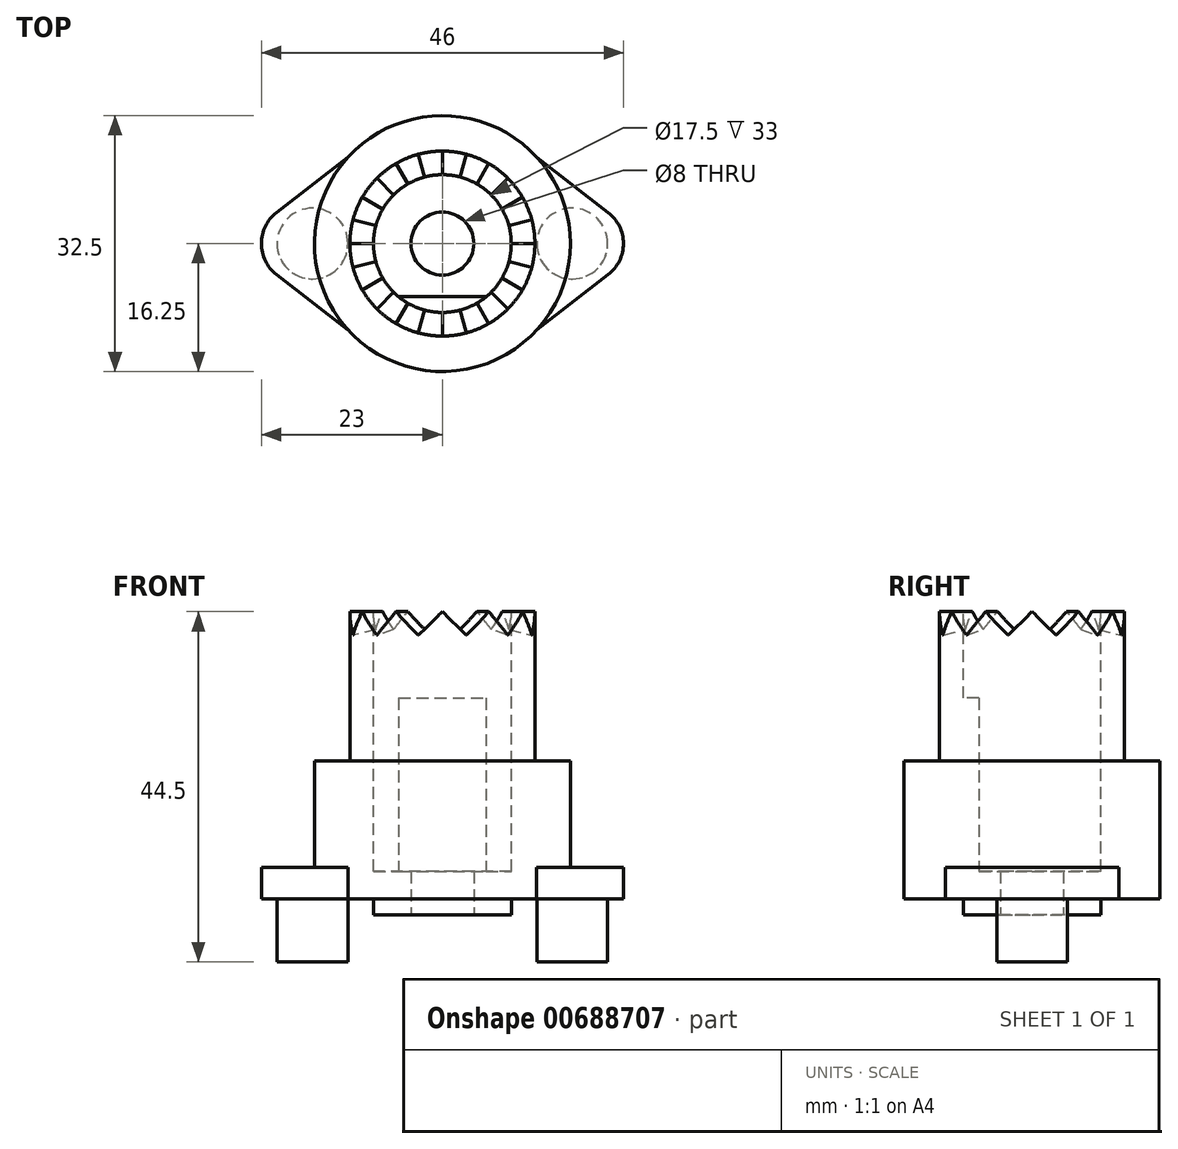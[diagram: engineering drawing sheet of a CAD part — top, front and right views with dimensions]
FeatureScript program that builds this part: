
annotation { "Feature Type Name" : "Feature", "Feature Type Description" : "" }
export const myFeature = defineFeature(function(context is Context, id is Id, definition is map)
    precondition{}
    {
        {
            var Q0;
            Q0=qCreatedBy(makeId("Top.planeOp"),FACE);
            var sketch = newSketch(context, id + "F0", { "sketchPlane" : qUnion([Q0])});
            skCircle(sketch, "E0", {"center": v(0, 0) * mm, "radius": 8.75 * mm});
            skSolve(sketch);
        }
        {
            var Q0;
            Q0 = qSketchRegion(id + "F0", true);
            extrude(context, id + "F1", {"entities" : qUnion([Q0]), "depth" : 2 * mm, "offsetDistance" : 25 * mm});
        }
        {
            var Q0;
            Q0=makeQuery(id+"F1.opExtrude","CAP_FACE",FACE,{"disambiguationData":[OSD([sQuery(id+"F0.wireOp",EDGE,"E0")])],"isStart":false});
            var sketch = newSketch(context, id + "F2", { "sketchPlane" : qUnion([Q0])});
            skCircle(sketch, "E1", {"center": v(0, 0) * mm, "radius": 16.25 * mm});
            skSolve(sketch);
        }
        {
            var Q0;
            Q0 = qSketchRegion(id + "F2", true);
            extrude(context, id + "F3", {"entities" : qUnion([Q0]), "operationType" : NewBodyOperationType.ADD, "depth" : 17.5 * mm, "offsetDistance" : 25 * mm});
        }
        {
            var Q0;
            Q0=makeQuery(id+"F3.opExtrude","CAP_FACE",FACE,{"disambiguationData":[OSD([sQuery(id+"F2.wireOp",EDGE,"E1")])],"isStart":false});
            var sketch = newSketch(context, id + "F4", { "sketchPlane" : qUnion([Q0])});
            skCircle(sketch, "E2", {"center": v(0, 0) * mm, "radius": 11.75 * mm});
            skSolve(sketch);
        }
        {
            var Q0;
            Q0=makeQuery(id+"F4.imprint","IMPRINT",FACE,{"disambiguationData":[TD([[makeQuery(id+"F4.imprint","IMPRINT",EDGE,{"derivedFrom":sQuery(id+"F4.wireOp",EDGE,"E2")}),1.0]])]});
            extrude(context, id + "F5", {"entities" : qUnion([Q0]), "operationType" : NewBodyOperationType.ADD, "depth" : 19 * mm, "offsetDistance" : 25 * mm});
        }
        {
            var Q0;
            Q0=makeQuery(id+"F5.opExtrude","CAP_FACE",FACE,{"disambiguationData":[OSD([sQuery(id+"F4.wireOp",EDGE,"E2")])],"isStart":false});
            var sketch = newSketch(context, id + "F6", { "sketchPlane" : qUnion([Q0])});
            skCircle(sketch, "E3", {"center": v(0, 0) * mm, "radius": 8.75 * mm});
            skSolve(sketch);
        }
        {
            var Q0;
            Q0=makeQuery(id+"F6.imprint","IMPRINT",FACE,{"disambiguationData":[TD([[makeQuery(id+"F6.imprint","IMPRINT",EDGE,{"derivedFrom":sQuery(id+"F6.wireOp",EDGE,"E3")}),1.0]])]});
            extrude(context, id + "F7", {"entities" : qUnion([Q0]), "operationType" : NewBodyOperationType.REMOVE, "oppositeDirection" : true, "depth" : 33 * mm, "offsetDistance" : 25 * mm});
        }
        {
            var Q0;
            Q0=makeQuery(id+"F1.opExtrude","CAP_FACE",FACE,{"disambiguationData":[OSD([sQuery(id+"F0.wireOp",EDGE,"E0")])],"isStart":true});
            var sketch = newSketch(context, id + "F8", { "sketchPlane" : qUnion([Q0])});
            skCircle(sketch, "E4", {"center": v(0, 0) * mm, "radius": 4 * mm});
            skSolve(sketch);
        }
        {
            var Q0;
            Q0=makeQuery(id+"F8.imprint","IMPRINT",FACE,{"disambiguationData":[TD([[makeQuery(id+"F8.imprint","IMPRINT",EDGE,{"derivedFrom":sQuery(id+"F8.wireOp",EDGE,"E4")}),1.0]])]});
            extrude(context, id + "F9", {"entities" : qUnion([Q0]), "operationType" : NewBodyOperationType.REMOVE, "endBound" : BoundingType.UP_TO_NEXT, "oppositeDirection" : true, "depth" : 25 * mm, "offsetDistance" : 25 * mm});
        }
        {
            var Q0;
            Q0=makeQuery(id+"F3.opExtrude","CAP_FACE",FACE,{"disambiguationData":[OSD([sQuery(id+"F2.wireOp",EDGE,"E1")])],"isStart":true});
            var sketch = newSketch(context, id + "F10", { "sketchPlane" : qUnion([Q0])});
            skLineSegment(sketch, "E5", {"start": v(-11.96, 11) * mm, "end": v(-21.06, 3.95) * mm});
            skLineSegment(sketch, "E6", {"start": v(-21.06, -3.95) * mm, "end": v(-11.96, -11) * mm});
            skArc(sketch, "E7.filletArc", {"start": v(-21.06, 3.95) * mm, "mid": v(-23, 0) * mm, "end": v(-21.06, -3.95) * mm});
            skLineSegment(sketch, "E8", {"start": v(11.96, -11) * mm, "end": v(21.06, -3.95) * mm});
            skLineSegment(sketch, "E9", {"start": v(21.06, 3.95) * mm, "end": v(11.96, 11) * mm});
            skArc(sketch, "E10.filletArc", {"start": v(21.06, -3.95) * mm, "mid": v(23, 0) * mm, "end": v(21.06, 3.95) * mm});
            skLineSegment(sketch, "E11", {"start": v(-18, 0) * mm, "end": v(0, 0) * mm, "construction": true});
            skArc(sketch, "E12", {"start": v(11.96, -11) * mm, "mid": v(16.25, 0) * mm, "end": v(11.96, 11) * mm});
            skArc(sketch, "E13", {"start": v(-11.96, 11) * mm, "mid": v(-16.25, 0) * mm, "end": v(-11.96, -11) * mm});
            skSolve(sketch);
        }
        {
            var Q0;
            {var subQ0=sQuery(id+"F10.wireOp",EDGE,"E7.filletArc");Q0=makeQuery(id+"F10.imprint","IMPRINT",FACE,{"disambiguationData":[TD([[makeQuery(id+"F10.imprint","IMPRINT",EDGE,{"derivedFrom":subQ0}),1.0]])]});}
            var Q1;
            {var subQ0=sQuery(id+"F10.wireOp",EDGE,"E10.filletArc");Q1=makeQuery(id+"F10.imprint","IMPRINT",FACE,{"disambiguationData":[TD([[makeQuery(id+"F10.imprint","IMPRINT",EDGE,{"derivedFrom":subQ0}),1.0]])]});}
            var Q2;
            Q2=sQuery(id+"F10.wireOp",EDGE,"E5");
            var Q3;
            Q3=sQuery(id+"F10.wireOp",EDGE,"E13");
            var Q4;
            Q4=sQuery(id+"F10.wireOp",EDGE,"E7.filletArc");
            var Q5;
            Q5=sQuery(id+"F10.wireOp",EDGE,"E6");
            extrude(context, id + "F11", {"entities" : qUnion([Q0, Q1]), "operationType" : NewBodyOperationType.ADD, "surfaceEntities" : qUnion([Q2, Q3, Q4, Q5]), "oppositeDirection" : true, "depth" : 4 * mm, "offsetDistance" : 25 * mm});
        }
        {
            var Q0;
            Q0=makeQuery(id+"F11.boolean.opBoolean","MERGE",FACE,{"derivedFrom":[makeQuery(id+"F3.opExtrude","CAP_FACE",FACE,{"disambiguationData":[OSD([sQuery(id+"F2.wireOp",EDGE,"E1")])],"isStart":true}),makeQuery(id+"F11.opExtrude","CAP_FACE",FACE,{"disambiguationData":[OSD([sQuery(id+"F10.wireOp",EDGE,"E5"),sQuery(id+"F10.wireOp",EDGE,"E6"),sQuery(id+"F10.wireOp",EDGE,"E7.filletArc"),sQuery(id+"F10.wireOp",EDGE,"E13")])],"isStart":true}),makeQuery(id+"F11.opExtrude","CAP_FACE",FACE,{"disambiguationData":[OSD([sQuery(id+"F10.wireOp",EDGE,"E8"),sQuery(id+"F10.wireOp",EDGE,"E9"),sQuery(id+"F10.wireOp",EDGE,"E10.filletArc"),sQuery(id+"F10.wireOp",EDGE,"E12")])],"isStart":true})]});
            var sketch = newSketch(context, id + "F12", { "sketchPlane" : qUnion([Q0])});
            skCircle(sketch, "E14", {"center": v(16.5, 0) * mm, "radius": 4.5 * mm});
            skLineSegment(sketch, "E15", {"start": v(23, 0) * mm, "end": v(-23, 0) * mm, "construction": true});
            skCircle(sketch, "E16.1.0", {"center": v(-16.5, 0) * mm, "radius": 4.5 * mm});
            skPoint(sketch, "E16.center", {"position": v(0, 0) * mm});
            skSolve(sketch);
        }
        {
            var Q0;
            Q0=makeQuery(id+"F12.imprint","IMPRINT",FACE,{"disambiguationData":[TD([[makeQuery(id+"F12.imprint","IMPRINT",EDGE,{"derivedFrom":sQuery(id+"F12.wireOp",EDGE,"E16.1.0")}),1.0]])]});
            var Q1;
            Q1=makeQuery(id+"F12.imprint","IMPRINT",FACE,{"disambiguationData":[TD([[makeQuery(id+"F12.imprint","IMPRINT",EDGE,{"derivedFrom":sQuery(id+"F12.wireOp",EDGE,"E14")}),1.0]])]});
            extrude(context, id + "F13", {"entities" : qUnion([Q0, Q1]), "operationType" : NewBodyOperationType.ADD, "depth" : 8 * mm, "offsetDistance" : 25 * mm});
        }
        {
            var Q0;
            Q0=makeQuery(id+"F7.boolean.opBoolean","COPY",FACE,{"derivedFrom":makeQuery(id+"F7.opExtrude","CAP_FACE",FACE,{"disambiguationData":[OSD([sQuery(id+"F6.wireOp",EDGE,"E3")])],"isStart":false})});
            var sketch = newSketch(context, id + "F14", { "sketchPlane" : qUnion([Q0])});
            skLineSegment(sketch, "E17", {"start": v(-5.57, -6.75) * mm, "end": v(5.57, -6.75) * mm});
            skSolve(sketch);
        }
        {
            var Q0;
            {var subQ0=sQuery(id+"F14.wireOp",EDGE,"E17");Q0=makeQuery(id+"F14.imprint","IMPRINT",FACE,{"disambiguationData":[TD([[makeQuery(id+"F14.imprint","IMPRINT",EDGE,{"derivedFrom":subQ0}),-1.0]])]});}
            extrude(context, id + "F15", {"entities" : qUnion([Q0]), "operationType" : NewBodyOperationType.ADD, "depth" : 22 * mm, "offsetDistance" : 25 * mm});
        }
        {
            var Q0;
            Q0=makeQuery(id+"F5.opExtrude","CAP_FACE",FACE,{"disambiguationData":[OSD([sQuery(id+"F4.wireOp",EDGE,"E2")])],"isStart":false});
            var sketch = newSketch(context, id + "F16", { "sketchPlane" : qUnion([Q0])});
            skLineSegment(sketch, "E18", {"start": v(-8.75, 0) * mm, "end": v(-11.75, 0) * mm});
            skLineSegment(sketch, "E19.1.0", {"start": v(-7.58, -4.37) * mm, "end": v(-10.18, -5.87) * mm});
            skLineSegment(sketch, "E19.2.0", {"start": v(-4.38, -7.58) * mm, "end": v(-5.88, -10.18) * mm});
            skLineSegment(sketch, "E19.3.0", {"start": v(0, -8.75) * mm, "end": v(0, -11.75) * mm});
            skLineSegment(sketch, "E19.4.0", {"start": v(4.37, -7.58) * mm, "end": v(5.87, -10.18) * mm});
            skLineSegment(sketch, "E19.5.0", {"start": v(7.58, -4.37) * mm, "end": v(10.18, -5.87) * mm});
            skLineSegment(sketch, "E19.6.0", {"start": v(8.75, 0) * mm, "end": v(11.75, 0) * mm});
            skLineSegment(sketch, "E19.7.0", {"start": v(7.58, 4.37) * mm, "end": v(10.18, 5.87) * mm});
            skLineSegment(sketch, "E19.8.0", {"start": v(4.38, 7.58) * mm, "end": v(5.88, 10.18) * mm});
            skLineSegment(sketch, "E19.9.0", {"start": v(0, 8.75) * mm, "end": v(0, 11.75) * mm});
            skLineSegment(sketch, "E19.10.0", {"start": v(-4.38, 7.58) * mm, "end": v(-5.88, 10.18) * mm});
            skLineSegment(sketch, "E19.11.0", {"start": v(-7.58, 4.38) * mm, "end": v(-10.18, 5.88) * mm});
            skPoint(sketch, "E19.center", {"position": v(0, 0) * mm});
            skSolve(sketch);
        }
        {
            var Q0;
            {var subQ0=sQuery(id+"F16.wireOp",EDGE,"E18");Q0=makeQuery(id+"F16.imprint","IMPRINT",FACE,{"disambiguationData":[TD([[makeQuery(id+"F16.imprint","IMPRINT",EDGE,{"derivedFrom":subQ0}),1.0]])]});}
            extrude(context, id + "F17", {"entities" : qUnion([Q0]), "operationType" : NewBodyOperationType.REMOVE, "oppositeDirection" : true, "depth" : 3 * mm, "offsetDistance" : 25 * mm});
        }
        {
            var Q0;
            Q0=makeQuery(id+"F17.boolean.opBoolean","COPY",EDGE,{"derivedFrom":makeQuery(id+"F17.opExtrude","CAP_EDGE",EDGE,{"disambiguationData":[OSD([sQuery(id+"F16.wireOp",EDGE,"E18")])],"isStart":false})});
            chamfer(context, id + "F18", {"entities" : qUnion([Q0]), "width" : 3 * mm, "tangentPropagation" : true});
        }
        {
            var Q0;
            Q0=makeQuery(id+"F17.boolean.opBoolean","COPY",EDGE,{"derivedFrom":makeQuery(id+"F17.opExtrude","CAP_EDGE",EDGE,{"disambiguationData":[OSD([sQuery(id+"F16.wireOp",EDGE,"E19.1.0")])],"isStart":false})});
            chamfer(context, id + "F19", {"entities" : qUnion([Q0]), "width" : 3 * mm, "tangentPropagation" : true});
        }
        {
            var Q0;
            {var subQ0=sQuery(id+"F16.wireOp",EDGE,"E19.10.0");Q0=makeQuery(id+"F16.imprint","IMPRINT",FACE,{"disambiguationData":[TD([[makeQuery(id+"F16.imprint","IMPRINT",EDGE,{"derivedFrom":subQ0}),1.0]])]});}
            var Q1;
            {var subQ0=sQuery(id+"F16.wireOp",EDGE,"E19.8.0");Q1=makeQuery(id+"F16.imprint","IMPRINT",FACE,{"disambiguationData":[TD([[makeQuery(id+"F16.imprint","IMPRINT",EDGE,{"derivedFrom":subQ0}),1.0]])]});}
            var Q2;
            {var subQ0=sQuery(id+"F16.wireOp",EDGE,"E19.6.0");Q2=makeQuery(id+"F16.imprint","IMPRINT",FACE,{"disambiguationData":[TD([[makeQuery(id+"F16.imprint","IMPRINT",EDGE,{"derivedFrom":subQ0}),1.0]])]});}
            var Q3;
            {var subQ0=sQuery(id+"F16.wireOp",EDGE,"E19.4.0");Q3=makeQuery(id+"F16.imprint","IMPRINT",FACE,{"disambiguationData":[TD([[makeQuery(id+"F16.imprint","IMPRINT",EDGE,{"derivedFrom":subQ0}),1.0]])]});}
            var Q4;
            {var subQ0=sQuery(id+"F16.wireOp",EDGE,"E19.2.0");Q4=makeQuery(id+"F16.imprint","IMPRINT",FACE,{"disambiguationData":[TD([[makeQuery(id+"F16.imprint","IMPRINT",EDGE,{"derivedFrom":subQ0}),1.0]])]});}
            extrude(context, id + "F20", {"entities" : qUnion([Q0, Q1, Q2, Q3, Q4]), "operationType" : NewBodyOperationType.REMOVE, "oppositeDirection" : true, "depth" : 3 * mm, "offsetDistance" : 25 * mm});
        }
        {
            var Q0;
            Q0=makeQuery(id+"F20.boolean.opBoolean","COPY",EDGE,{"derivedFrom":makeQuery(id+"F20.opExtrude","CAP_EDGE",EDGE,{"disambiguationData":[OSD([sQuery(id+"F16.wireOp",EDGE,"E19.8.0")])],"isStart":false})});
            var Q1;
            Q1=makeQuery(id+"F20.boolean.opBoolean","COPY",EDGE,{"derivedFrom":makeQuery(id+"F20.opExtrude","CAP_EDGE",EDGE,{"disambiguationData":[OSD([sQuery(id+"F16.wireOp",EDGE,"E19.5.0")])],"isStart":false})});
            var Q2;
            Q2=makeQuery(id+"F20.boolean.opBoolean","COPY",EDGE,{"derivedFrom":makeQuery(id+"F20.opExtrude","CAP_EDGE",EDGE,{"disambiguationData":[OSD([sQuery(id+"F16.wireOp",EDGE,"E19.3.0")])],"isStart":false})});
            var Q3;
            Q3=makeQuery(id+"F20.boolean.opBoolean","COPY",EDGE,{"derivedFrom":makeQuery(id+"F20.opExtrude","CAP_EDGE",EDGE,{"disambiguationData":[OSD([sQuery(id+"F16.wireOp",EDGE,"E19.10.0")])],"isStart":false})});
            chamfer(context, id + "F21", {"entities" : qUnion([Q0, Q1, Q2, Q3]), "width" : 3 * mm, "tangentPropagation" : true});
        }
        {
            var Q0;
            Q0=makeQuery(id+"F20.boolean.opBoolean","COPY",EDGE,{"derivedFrom":makeQuery(id+"F20.opExtrude","CAP_EDGE",EDGE,{"disambiguationData":[OSD([sQuery(id+"F16.wireOp",EDGE,"E19.6.0")])],"isStart":false})});
            var Q1;
            Q1=makeQuery(id+"F20.boolean.opBoolean","COPY",EDGE,{"derivedFrom":makeQuery(id+"F20.opExtrude","CAP_EDGE",EDGE,{"disambiguationData":[OSD([sQuery(id+"F16.wireOp",EDGE,"E19.4.0")])],"isStart":false})});
            var Q2;
            Q2=makeQuery(id+"F20.boolean.opBoolean","COPY",EDGE,{"derivedFrom":makeQuery(id+"F20.opExtrude","CAP_EDGE",EDGE,{"disambiguationData":[OSD([sQuery(id+"F16.wireOp",EDGE,"E19.11.0")])],"isStart":false})});
            chamfer(context, id + "F22", {"entities" : qUnion([Q0, Q1, Q2]), "width" : 3 * mm, "tangentPropagation" : true});
        }
        {
            var Q0;
            Q0=makeQuery(id+"F20.boolean.opBoolean","COPY",EDGE,{"derivedFrom":makeQuery(id+"F20.opExtrude","CAP_EDGE",EDGE,{"disambiguationData":[OSD([sQuery(id+"F16.wireOp",EDGE,"E19.9.0")])],"isStart":false})});
            var Q1;
            Q1=makeQuery(id+"F20.boolean.opBoolean","COPY",EDGE,{"derivedFrom":makeQuery(id+"F20.opExtrude","CAP_EDGE",EDGE,{"disambiguationData":[OSD([sQuery(id+"F16.wireOp",EDGE,"E19.7.0")])],"isStart":false})});
            chamfer(context, id + "F23", {"entities" : qUnion([Q0, Q1]), "width" : 3 * mm, "tangentPropagation" : true});
        }
        {
            var Q0;
            Q0=makeQuery(id+"F20.boolean.opBoolean","COPY",EDGE,{"derivedFrom":makeQuery(id+"F20.opExtrude","CAP_EDGE",EDGE,{"disambiguationData":[OSD([sQuery(id+"F16.wireOp",EDGE,"E19.2.0")])],"isStart":false})});
            chamfer(context, id + "F24", {"entities" : qUnion([Q0]), "width" : 3 * mm, "tangentPropagation" : true});
        }
        {
            var Q0;
            {var subQ0=sQuery(id+"F4.wireOp",EDGE,"E2");Q0=makeQuery(id+"F20.boolean.opBoolean","SPLIT",FACE,{"disambiguationData":[TD([makeQuery(id+"F19.opChamfer","BLEND_FACE",FACE,{"disambiguationData":[OSD([sQuery(id+"F16.wireOp",EDGE,"E19.1.0")])]})])],"derivedFrom":makeQuery(id+"F5.opExtrude","CAP_FACE",FACE,{"disambiguationData":[OSD([subQ0])],"isStart":false})});}
            var Q1;
            {var subQ0=sQuery(id+"F4.wireOp",EDGE,"E2");Q1=makeQuery(id+"F20.boolean.opBoolean","SPLIT",FACE,{"disambiguationData":[TD([makeQuery(id+"F20.opExtrude","SWEPT_FACE",FACE,{"disambiguationData":[OSD([sQuery(id+"F16.wireOp",EDGE,"E19.3.0")])]})])],"derivedFrom":makeQuery(id+"F5.opExtrude","CAP_FACE",FACE,{"disambiguationData":[OSD([subQ0])],"isStart":false})});}
            var Q2;
            {var subQ0=sQuery(id+"F4.wireOp",EDGE,"E2");Q2=makeQuery(id+"F20.boolean.opBoolean","SPLIT",FACE,{"disambiguationData":[TD([makeQuery(id+"F20.opExtrude","SWEPT_FACE",FACE,{"disambiguationData":[OSD([sQuery(id+"F16.wireOp",EDGE,"E19.5.0")])]})])],"derivedFrom":makeQuery(id+"F5.opExtrude","CAP_FACE",FACE,{"disambiguationData":[OSD([subQ0])],"isStart":false})});}
            var Q3;
            {var subQ0=sQuery(id+"F4.wireOp",EDGE,"E2");Q3=makeQuery(id+"F20.boolean.opBoolean","SPLIT",FACE,{"disambiguationData":[TD([makeQuery(id+"F20.opExtrude","SWEPT_FACE",FACE,{"disambiguationData":[OSD([sQuery(id+"F16.wireOp",EDGE,"E19.7.0")])]})])],"derivedFrom":makeQuery(id+"F5.opExtrude","CAP_FACE",FACE,{"disambiguationData":[OSD([subQ0])],"isStart":false})});}
            var Q4;
            {var subQ0=sQuery(id+"F4.wireOp",EDGE,"E2");Q4=makeQuery(id+"F20.boolean.opBoolean","SPLIT",FACE,{"disambiguationData":[TD([makeQuery(id+"F20.opExtrude","SWEPT_FACE",FACE,{"disambiguationData":[OSD([sQuery(id+"F16.wireOp",EDGE,"E19.9.0")])]})])],"derivedFrom":makeQuery(id+"F5.opExtrude","CAP_FACE",FACE,{"disambiguationData":[OSD([subQ0])],"isStart":false})});}
            var Q5;
            {var subQ0=sQuery(id+"F4.wireOp",EDGE,"E2");Q5=makeQuery(id+"F20.boolean.opBoolean","SPLIT",FACE,{"disambiguationData":[TD([makeQuery(id+"F18.opChamfer","BLEND_FACE",FACE,{"disambiguationData":[OSD([sQuery(id+"F16.wireOp",EDGE,"E18")])]})])],"derivedFrom":makeQuery(id+"F5.opExtrude","CAP_FACE",FACE,{"disambiguationData":[OSD([subQ0])],"isStart":false})});}
            extrude(context, id + "F25", {"entities" : qUnion([Q0, Q1, Q2, Q3, Q4, Q5]), "operationType" : NewBodyOperationType.REMOVE, "oppositeDirection" : true, "depth" : 3 * mm, "offsetDistance" : 25 * mm});
        }
        {
            var Q0;
            Q0=makeQuery(id+"F25.boolean.opBoolean","COPY",EDGE,{"derivedFrom":makeQuery(id+"F25.opExtrude","CAP_EDGE",EDGE,{"disambiguationData":[OSD([sQuery(id+"F4.wireOp",EDGE,"E2"),sQuery(id+"F16.wireOp",EDGE,"E19.11.0")])],"isStart":false})});
            var Q1;
            Q1=makeQuery(id+"F25.boolean.opBoolean","COPY",EDGE,{"derivedFrom":makeQuery(id+"F25.opExtrude","CAP_EDGE",EDGE,{"disambiguationData":[OSD([sQuery(id+"F4.wireOp",EDGE,"E2"),sQuery(id+"F16.wireOp",EDGE,"E19.1.0")])],"isStart":false})});
            var Q2;
            Q2=makeQuery(id+"F25.boolean.opBoolean","COPY",EDGE,{"derivedFrom":makeQuery(id+"F25.opExtrude","CAP_EDGE",EDGE,{"disambiguationData":[OSD([sQuery(id+"F4.wireOp",EDGE,"E2"),sQuery(id+"F16.wireOp",EDGE,"E19.4.0")])],"isStart":false})});
            var Q3;
            Q3=makeQuery(id+"F25.boolean.opBoolean","COPY",EDGE,{"derivedFrom":makeQuery(id+"F25.opExtrude","CAP_EDGE",EDGE,{"disambiguationData":[OSD([sQuery(id+"F4.wireOp",EDGE,"E2"),sQuery(id+"F16.wireOp",EDGE,"E19.6.0")])],"isStart":false})});
            var Q4;
            Q4=makeQuery(id+"F25.boolean.opBoolean","COPY",EDGE,{"derivedFrom":makeQuery(id+"F25.opExtrude","CAP_EDGE",EDGE,{"disambiguationData":[OSD([sQuery(id+"F4.wireOp",EDGE,"E2"),sQuery(id+"F16.wireOp",EDGE,"E19.9.0")])],"isStart":false})});
            var Q5;
            Q5=makeQuery(id+"F25.boolean.opBoolean","COPY",EDGE,{"derivedFrom":makeQuery(id+"F25.opExtrude","CAP_EDGE",EDGE,{"disambiguationData":[OSD([sQuery(id+"F4.wireOp",EDGE,"E2"),sQuery(id+"F16.wireOp",EDGE,"E19.7.0")])],"isStart":false})});
            var Q6;
            Q6=makeQuery(id+"F25.boolean.opBoolean","COPY",EDGE,{"derivedFrom":makeQuery(id+"F25.opExtrude","CAP_EDGE",EDGE,{"disambiguationData":[OSD([sQuery(id+"F4.wireOp",EDGE,"E2"),sQuery(id+"F16.wireOp",EDGE,"E19.2.0")])],"isStart":false})});
            var Q7;
            Q7=makeQuery(id+"F25.boolean.opBoolean","COPY",EDGE,{"derivedFrom":makeQuery(id+"F25.opExtrude","CAP_EDGE",EDGE,{"disambiguationData":[OSD([sQuery(id+"F4.wireOp",EDGE,"E2"),sQuery(id+"F16.wireOp",EDGE,"E18")])],"isStart":false})});
            var Q8;
            Q8=makeQuery(id+"F25.boolean.opBoolean","COPY",EDGE,{"derivedFrom":makeQuery(id+"F25.opExtrude","CAP_EDGE",EDGE,{"disambiguationData":[OSD([sQuery(id+"F4.wireOp",EDGE,"E2"),sQuery(id+"F16.wireOp",EDGE,"E19.5.0")])],"isStart":false})});
            var Q9;
            Q9=makeQuery(id+"F25.boolean.opBoolean","COPY",EDGE,{"derivedFrom":makeQuery(id+"F25.opExtrude","CAP_EDGE",EDGE,{"disambiguationData":[OSD([sQuery(id+"F4.wireOp",EDGE,"E2"),sQuery(id+"F16.wireOp",EDGE,"E19.3.0")])],"isStart":false})});
            var Q10;
            Q10=makeQuery(id+"F25.boolean.opBoolean","COPY",EDGE,{"derivedFrom":makeQuery(id+"F25.opExtrude","CAP_EDGE",EDGE,{"disambiguationData":[OSD([sQuery(id+"F4.wireOp",EDGE,"E2"),sQuery(id+"F16.wireOp",EDGE,"E19.10.0")])],"isStart":false})});
            var Q11;
            Q11=makeQuery(id+"F25.boolean.opBoolean","COPY",EDGE,{"derivedFrom":makeQuery(id+"F25.opExtrude","CAP_EDGE",EDGE,{"disambiguationData":[OSD([sQuery(id+"F4.wireOp",EDGE,"E2"),sQuery(id+"F16.wireOp",EDGE,"E19.8.0")])],"isStart":false})});
            chamfer(context, id + "F26", {"entities" : qUnion([Q0, Q1, Q2, Q3, Q4, Q5, Q6, Q7, Q8, Q9, Q10, Q11]), "width" : 3 * mm, "tangentPropagation" : true});
        }
    });
